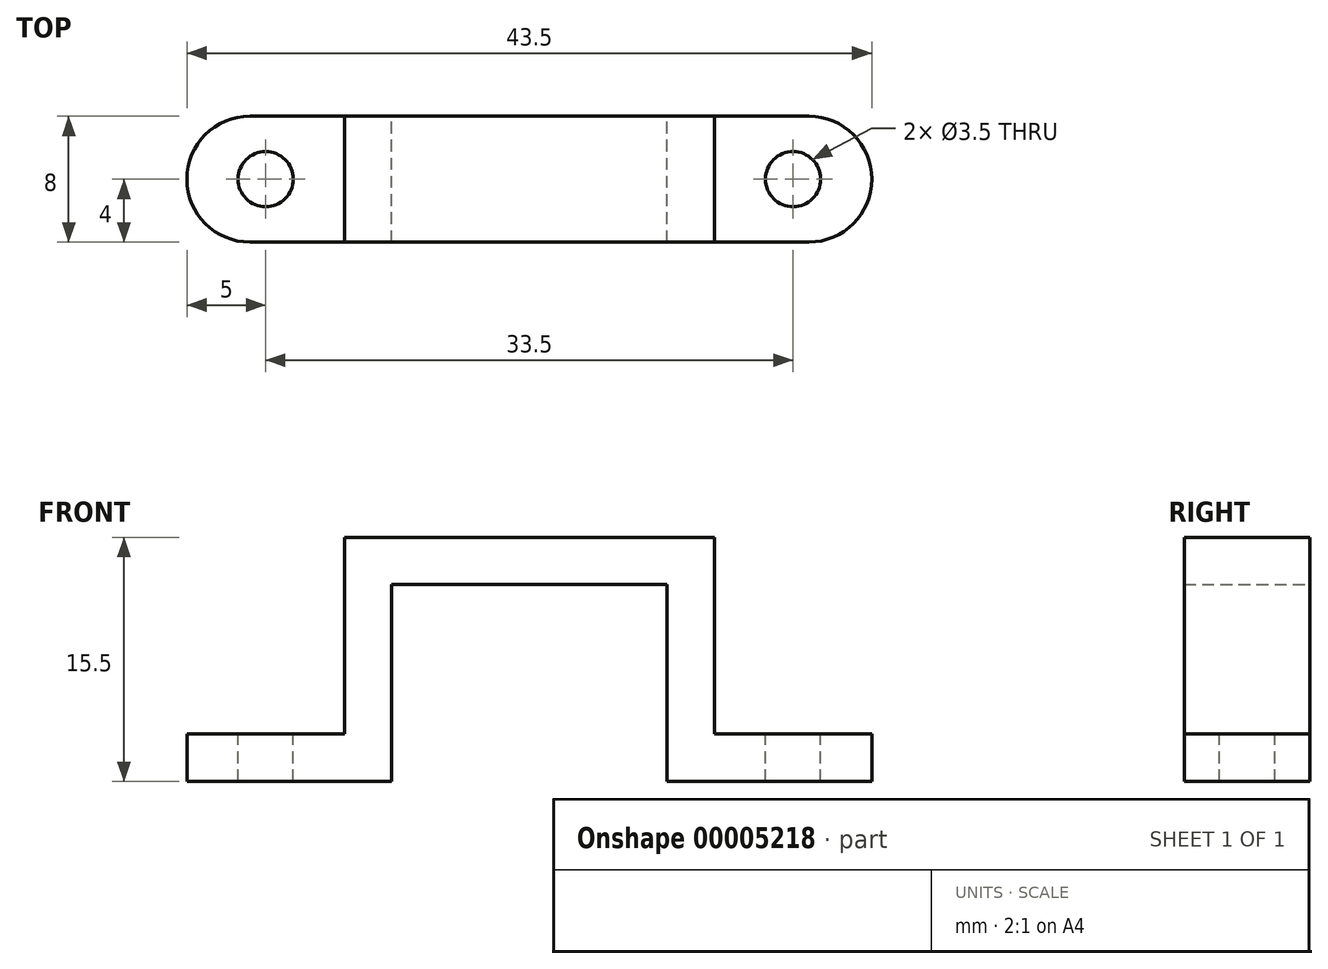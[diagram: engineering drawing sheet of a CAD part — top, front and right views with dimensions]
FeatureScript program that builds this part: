
annotation { "Feature Type Name" : "Feature", "Feature Type Description" : "" }
export const myFeature = defineFeature(function(context is Context, id is Id, definition is map)
    precondition{}
    {
        {
            var Q0;
            Q0=qCreatedBy(makeId("Front.planeOp"),FACE);
            var sketch = newSketch(context, id + "F0", { "sketchPlane" : qUnion([Q0])});
            skLineSegment(sketch, "E0", {"start": v(0, 0) * mm, "end": v(0, 12.5) * mm, "construction": true});
            skLineSegment(sketch, "E1", {"start": v(-8.75, 12.5) * mm, "end": v(-8.75, 0) * mm});
            skLineSegment(sketch, "E2", {"start": v(-8.75, 0) * mm, "end": v(-21.75, 0) * mm});
            skLineSegment(sketch, "E3", {"start": v(-21.75, 0) * mm, "end": v(-21.75, 3) * mm});
            skLineSegment(sketch, "E4", {"start": v(-21.75, 3) * mm, "end": v(-11.75, 3) * mm});
            skLineSegment(sketch, "E5", {"start": v(-11.75, 3) * mm, "end": v(-11.75, 15.5) * mm});
            skLineSegment(sketch, "E6.MirrorCS", {"start": v(8.75, 0) * mm, "end": v(21.75, 0) * mm});
            skLineSegment(sketch, "E7.MirrorCS", {"start": v(21.75, 0) * mm, "end": v(21.75, 3) * mm});
            skLineSegment(sketch, "E8.MirrorCS", {"start": v(21.75, 3) * mm, "end": v(11.75, 3) * mm});
            skLineSegment(sketch, "E9.MirrorCS", {"start": v(8.75, 12.5) * mm, "end": v(8.75, 0) * mm});
            skLineSegment(sketch, "E10.MirrorCS", {"start": v(11.75, 3) * mm, "end": v(11.75, 15.5) * mm});
            skLineSegment(sketch, "E11", {"start": v(-8.75, 12.5) * mm, "end": v(8.75, 12.5) * mm});
            skLineSegment(sketch, "E12", {"start": v(-11.75, 15.5) * mm, "end": v(11.75, 15.5) * mm});
            skSolve(sketch);
        }
        {
            var Q0;
            Q0 = qSketchRegion(id + "F0", true);
            extrude(context, id + "F1", {"entities" : qUnion([Q0]), "depth" : 8 * mm, "symmetric" : true});
        }
        {
            var Q0;
            Q0=makeQuery(id+"F1.opExtrude","SWEPT_FACE",FACE,{"disambiguationData":[OSD([sQuery(id+"F0.wireOp",EDGE,"E4")])]});
            var sketch = newSketch(context, id + "F2", { "sketchPlane" : qUnion([Q0])});
            skLineSegment(sketch, "E13", {"start": v(-21.75, 0) * mm, "end": v(-11.75, 0) * mm, "construction": true});
            skCircle(sketch, "E14", {"center": v(-16.75, 0) * mm, "radius": 1.75 * mm});
            skLineSegment(sketch, "E15", {"start": v(0, 0) * mm, "end": v(0, 8.07) * mm, "construction": true});
            skCircle(sketch, "E16.MirrorC", {"center": v(16.75, 0) * mm, "radius": 1.75 * mm});
            skSolve(sketch);
        }
        {
            var Q0;
            Q0 = qSketchRegion(id + "F2", true);
            extrude(context, id + "F3", {"entities" : qUnion([Q0]), "operationType" : NewBodyOperationType.REMOVE, "endBound" : BoundingType.THROUGH_ALL, "oppositeDirection" : true, "depth" : 25 * mm});
        }
        {
            var Q0;
            Q0=makeQuery(id+"F1.opExtrude","CAP_EDGE",EDGE,{"disambiguationData":[OSD([sQuery(id+"F0.wireOp",EDGE,"E3")])],"isStart":true});
            var Q1;
            Q1=makeQuery(id+"F1.opExtrude","CAP_EDGE",EDGE,{"disambiguationData":[OSD([sQuery(id+"F0.wireOp",EDGE,"E3")])],"isStart":false});
            var Q2;
            Q2=makeQuery(id+"F1.opExtrude","CAP_EDGE",EDGE,{"disambiguationData":[OSD([sQuery(id+"F0.wireOp",EDGE,"E7.MirrorCS")])],"isStart":false});
            var Q3;
            Q3=makeQuery(id+"F1.opExtrude","CAP_EDGE",EDGE,{"disambiguationData":[OSD([sQuery(id+"F0.wireOp",EDGE,"E7.MirrorCS")])],"isStart":true});
            fillet(context, id + "F4", {"entities" : qUnion([Q0, Q1, Q2, Q3]), "radius" : 4 * mm, "tangentPropagation" : true, "allowEdgeOverflow" : false});
        }
    });
